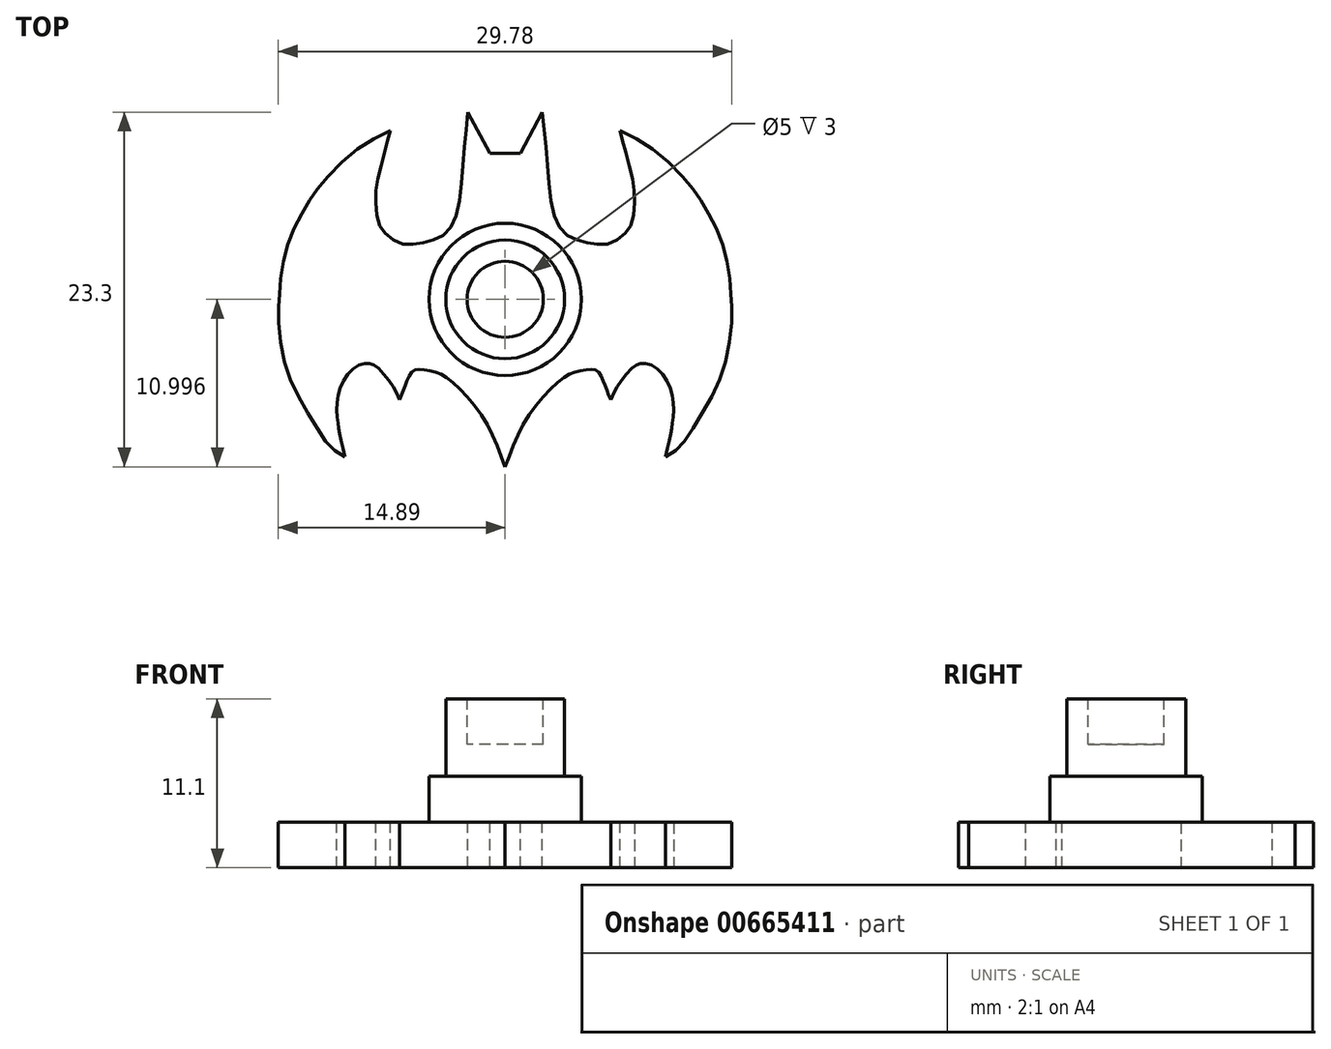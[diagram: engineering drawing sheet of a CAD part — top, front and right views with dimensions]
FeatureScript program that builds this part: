
annotation { "Feature Type Name" : "Feature", "Feature Type Description" : "" }
export const myFeature = defineFeature(function(context is Context, id is Id, definition is map)
    precondition{}
    {
        {
            var Q0;
            Q0=qCreatedBy(makeId("Top.planeOp"),FACE);
            var sketch = newSketch(context, id + "F0", { "sketchPlane" : qUnion([Q0])});
            skFitSpline(sketch, "E0", {"points": [v(0, -13.14) * mm, v(-1.56, -9.75) * mm, v(-3.7, -7.4) * mm, v(-4.68, -6.89) * mm, v(-5.61, -6.74) * mm, v(-6.04, -6.86) * mm, v(-6.39, -7.37) * mm, v(-6.64, -8.04) * mm, v(-6.93, -8.73) * mm], "startDerivative": vector(-5.93, 16.12) * mm, "endDerivative": vector(-3.07, -7.1) * mm});
            skFitSpline(sketch, "E1", {"points": [v(-6.93, -8.73) * mm, v(-7.58, -7.55) * mm, v(-8.5, -6.53) * mm, v(-9, -6.35) * mm, v(-9.85, -6.6) * mm, v(-10.76, -7.78) * mm, v(-11.06, -9.14) * mm, v(-10.98, -10.28) * mm, v(-10.88, -10.97) * mm, v(-10.52, -12.48) * mm], "startDerivative": vector(-4.6, 9.68) * mm, "endDerivative": vector(3.25, -12.82) * mm});
            skFitSpline(sketch, "E2", {"points": [v(-10.52, -12.48) * mm, v(-11.43, -11.87) * mm, v(-12.38, -10.55) * mm, v(-13.71, -8.27) * mm, v(-14.59, -5.78) * mm, v(-14.89, -2.97) * mm, v(-14.81, -1.67) * mm, v(-14.56, 0.42) * mm, v(-13.84, 2.55) * mm, v(-12.9, 4.27) * mm, v(-11.97, 5.54) * mm, v(-9.86, 7.6) * mm, v(-7.54, 8.95) * mm], "startDerivative": vector(-15.76, 8.46) * mm, "endDerivative": vector(24.77, 12.2) * mm});
            skFitSpline(sketch, "E3", {"points": [v(-7.54, 8.95) * mm, v(-7.86, 7.72) * mm, v(-8.34, 5.87) * mm, v(-8.5, 4.45) * mm, v(-8.32, 2.94) * mm, v(-7.86, 2.19) * mm, v(-6.93, 1.55) * mm, v(-5.88, 1.5) * mm, v(-4.82, 1.74) * mm, v(-3.8, 2.3) * mm, v(-3.1, 3.82) * mm, v(-2.76, 6.96) * mm, v(-2.44, 10.16) * mm], "startDerivative": vector(-3.77, -15.18) * mm, "endDerivative": vector(2.84, 26.23) * mm});
            skFitSpline(sketch, "E4", {"points": [v(-2.44, 10.16) * mm, v(-1, 7.44) * mm], "startDerivative": vector(1.45, -2.72) * mm, "endDerivative": vector(1.45, -2.72) * mm});
            skFitSpline(sketch, "E5", {"points": [v(-1, 7.44) * mm, v(0, 7.44) * mm], "startDerivative": vector(1, 0) * mm, "endDerivative": vector(1, 0) * mm});
            skFitSpline(sketch, "E6.MirrorCS", {"points": [v(2.44, 10.16) * mm, v(1, 7.44) * mm], "startDerivative": vector(-1.45, -2.72) * mm, "endDerivative": vector(-1.45, -2.72) * mm});
            skFitSpline(sketch, "E7.MirrorCS", {"points": [v(1, 7.44) * mm, v(0, 7.44) * mm], "startDerivative": vector(-1, 0) * mm, "endDerivative": vector(-1, 0) * mm});
            skFitSpline(sketch, "E8.MirrorCS", {"points": [v(0, -13.14) * mm, v(1.56, -9.75) * mm, v(3.7, -7.4) * mm, v(4.68, -6.89) * mm, v(5.61, -6.74) * mm, v(6.04, -6.86) * mm, v(6.39, -7.37) * mm, v(6.64, -8.04) * mm, v(6.93, -8.73) * mm], "startDerivative": vector(5.93, 16.12) * mm, "endDerivative": vector(3.07, -7.1) * mm});
            skFitSpline(sketch, "E9.MirrorCS", {"points": [v(6.93, -8.73) * mm, v(7.58, -7.55) * mm, v(8.5, -6.53) * mm, v(9, -6.35) * mm, v(9.85, -6.6) * mm, v(10.76, -7.78) * mm, v(11.06, -9.14) * mm, v(10.98, -10.28) * mm, v(10.88, -10.97) * mm, v(10.52, -12.48) * mm], "startDerivative": vector(4.6, 9.68) * mm, "endDerivative": vector(-3.25, -12.82) * mm});
            skFitSpline(sketch, "E10.MirrorCS", {"points": [v(7.54, 8.95) * mm, v(7.86, 7.72) * mm, v(8.34, 5.87) * mm, v(8.5, 4.45) * mm, v(8.32, 2.94) * mm, v(7.86, 2.19) * mm, v(6.93, 1.55) * mm, v(5.88, 1.5) * mm, v(4.82, 1.74) * mm, v(3.8, 2.3) * mm, v(3.1, 3.82) * mm, v(2.76, 6.96) * mm, v(2.44, 10.16) * mm], "startDerivative": vector(3.77, -15.18) * mm, "endDerivative": vector(-2.84, 26.23) * mm});
            skFitSpline(sketch, "E11.MirrorCS", {"points": [v(10.52, -12.48) * mm, v(11.43, -11.87) * mm, v(12.38, -10.55) * mm, v(13.71, -8.27) * mm, v(14.59, -5.78) * mm, v(14.89, -2.97) * mm, v(14.81, -1.67) * mm, v(14.56, 0.42) * mm, v(13.84, 2.55) * mm, v(12.9, 4.27) * mm, v(11.97, 5.54) * mm, v(9.86, 7.6) * mm, v(7.54, 8.95) * mm], "startDerivative": vector(15.76, 8.46) * mm, "endDerivative": vector(-24.77, 12.2) * mm});
            skLineSegment(sketch, "E12", {"start": v(0, -13.14) * mm, "end": v(0, -2.14) * mm, "construction": true});
            skCircle(sketch, "E13", {"center": v(0, -2.14) * mm, "radius": 5 * mm});
            skCircle(sketch, "E14", {"center": v(0, -2.14) * mm, "radius": 3.9 * mm});
            skSolve(sketch);
        }
        {
            var Q0;
            Q0=makeQuery(id+"F0.imprint","IMPRINT",FACE,{"disambiguationData":[TD([[makeQuery(id+"F0.imprint","IMPRINT",EDGE,{"derivedFrom":sQuery(id+"F0.wireOp",EDGE,"E13")}),1.0]])]});
            extrude(context, id + "F1", {"entities" : qUnion([Q0]), "depth" : 3 * mm, "offsetDistance" : 25 * mm});
        }
        {
            var Q0;
            Q0=makeQuery(id+"F0.imprint","IMPRINT",FACE,{"disambiguationData":[TD([[makeQuery(id+"F0.imprint","IMPRINT",EDGE,{"derivedFrom":sQuery(id+"F0.wireOp",EDGE,"E14")}),1.0]])]});
            extrude(context, id + "F2", {"entities" : qUnion([Q0]), "operationType" : NewBodyOperationType.ADD, "depth" : 8.1 * mm, "offsetDistance" : 25 * mm});
        }
        {
            var Q0;
            Q0=makeQuery(id+"F0.imprint","IMPRINT",FACE,{"disambiguationData":[TD([[makeQuery(id+"F0.imprint","IMPRINT",EDGE,{"derivedFrom":sQuery(id+"F0.wireOp",EDGE,"E0")}),-1.0]])]});
            var Q1;
            Q1=makeQuery(id+"F0.imprint","IMPRINT",FACE,{"disambiguationData":[TD([[makeQuery(id+"F0.imprint","IMPRINT",EDGE,{"derivedFrom":sQuery(id+"F0.wireOp",EDGE,"E14")}),1.0]])]});
            var Q2;
            Q2=makeQuery(id+"F0.imprint","IMPRINT",FACE,{"disambiguationData":[TD([[makeQuery(id+"F0.imprint","IMPRINT",EDGE,{"derivedFrom":sQuery(id+"F0.wireOp",EDGE,"E13")}),1.0]])]});
            extrude(context, id + "F3", {"entities" : qUnion([Q0, Q1, Q2]), "operationType" : NewBodyOperationType.ADD, "oppositeDirection" : true, "depth" : 3 * mm, "offsetDistance" : 25 * mm});
        }
        {
            var Q0;
            Q0=makeQuery(id+"F2.opExtrude","CAP_FACE",FACE,{"disambiguationData":[OSD([sQuery(id+"F0.wireOp",EDGE,"E14")])],"isStart":false});
            var sketch = newSketch(context, id + "F4", { "sketchPlane" : qUnion([Q0])});
            skCircle(sketch, "E15", {"center": v(0, -2.14) * mm, "radius": 2.5 * mm});
            skSolve(sketch);
        }
        {
            var Q0;
            Q0=makeQuery(id+"F4.imprint","IMPRINT",FACE,{"disambiguationData":[TD([[makeQuery(id+"F4.imprint","IMPRINT",EDGE,{"derivedFrom":sQuery(id+"F4.wireOp",EDGE,"E15")}),1.0]])]});
            extrude(context, id + "F5", {"entities" : qUnion([Q0]), "operationType" : NewBodyOperationType.REMOVE, "oppositeDirection" : true, "depth" : 3 * mm, "offsetDistance" : 25 * mm});
        }
    });
